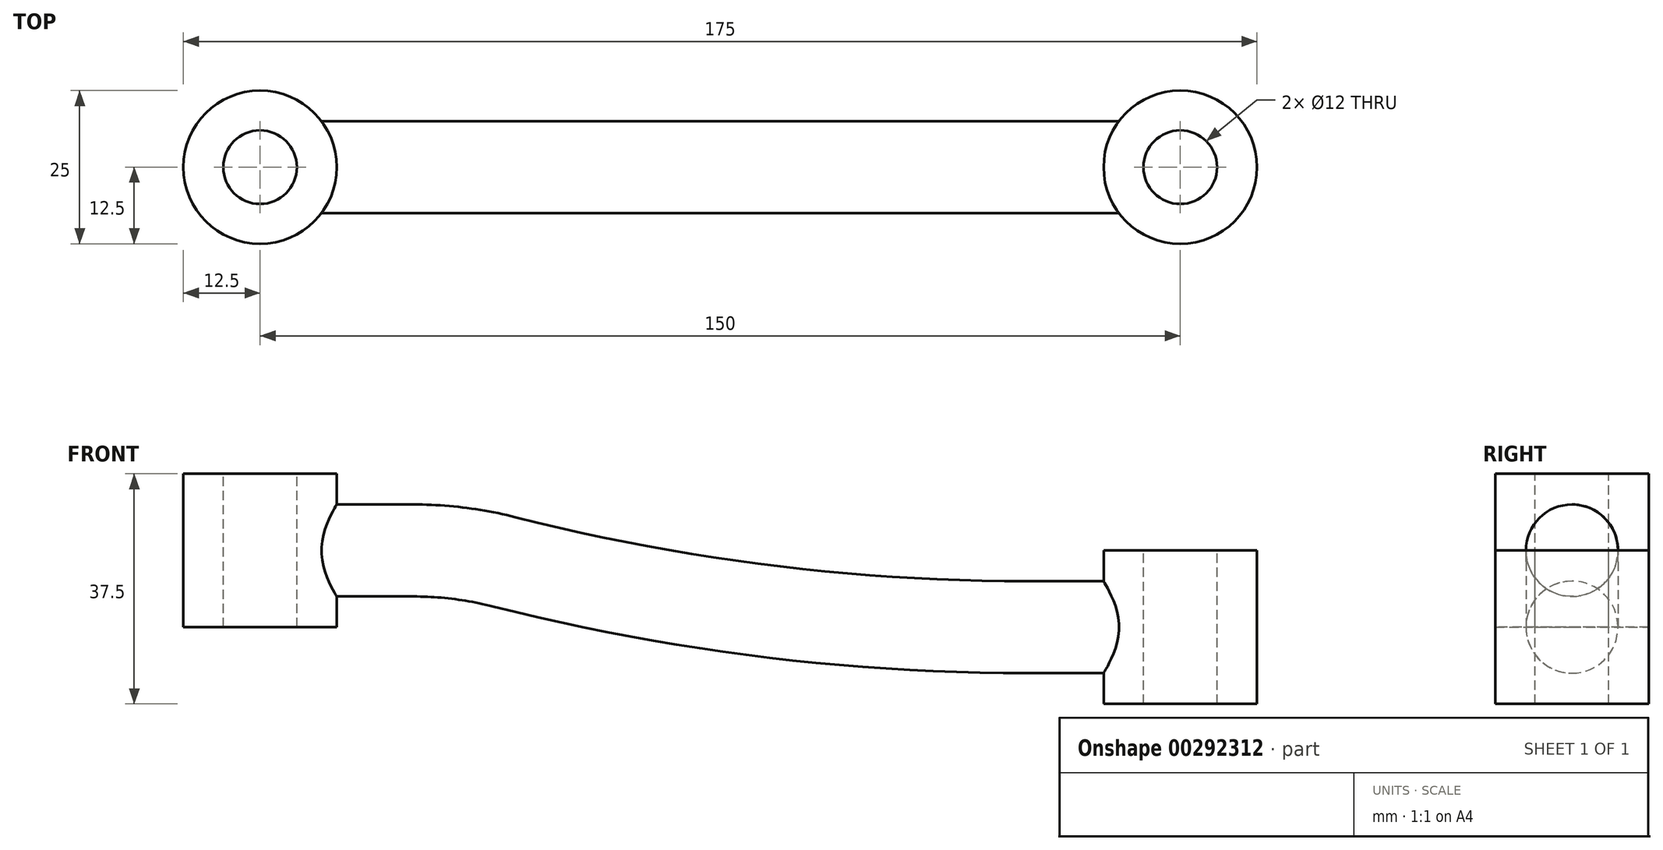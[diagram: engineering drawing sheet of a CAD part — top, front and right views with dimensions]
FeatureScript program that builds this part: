
annotation { "Feature Type Name" : "Feature", "Feature Type Description" : "" }
export const myFeature = defineFeature(function(context is Context, id is Id, definition is map)
    precondition{}
    {
        {
            var Q0;
            Q0=qCreatedBy(makeId("Top.planeOp"),FACE);
            var sketch = newSketch(context, id + "F0", { "sketchPlane" : qUnion([Q0])});
            skCircle(sketch, "E0", {"center": v(0, 0) * mm, "radius": 12.5 * mm});
            skCircle(sketch, "E1", {"center": v(150, 0) * mm, "radius": 12.5 * mm});
            skSolve(sketch);
        }
        {
            var Q0;
            Q0=makeQuery(id+"F0.imprint","IMPRINT",FACE,{"disambiguationData":[TD([[makeQuery(id+"F0.imprint","IMPRINT",EDGE,{"derivedFrom":sQuery(id+"F0.wireOp",EDGE,"E0")}),1.0]])]});
            extrude(context, id + "F1", {"entities" : qUnion([Q0]), "depth" : 25 * mm});
        }
        {
            var Q0;
            Q0=makeQuery(id+"F0.imprint","IMPRINT",FACE,{"disambiguationData":[TD([[makeQuery(id+"F0.imprint","IMPRINT",EDGE,{"derivedFrom":sQuery(id+"F0.wireOp",EDGE,"E1")}),1.0]])]});
            extrude(context, id + "F2", {"entities" : qUnion([Q0]), "endBound" : BoundingType.SYMMETRIC, "depth" : 25 * mm});
        }
        {
            var Q0;
            Q0=qCreatedBy(makeId("Front.planeOp"),FACE);
            var sketch = newSketch(context, id + "F3", { "sketchPlane" : qUnion([Q0])});
            skLineSegment(sketch, "E2", {"start": v(0, 12.5) * mm, "end": v(25, 12.5) * mm});
            skLineSegment(sketch, "E3", {"start": v(150, 0) * mm, "end": v(125, 0) * mm});
            skArc(sketch, "E4", {"start": v(39.77, 10.65) * mm, "mid": v(32.44, 12.04) * mm, "end": v(25, 12.5) * mm});
            skArc(sketch, "E5", {"start": v(39.77, 10.65) * mm, "mid": v(82.05, 2.67) * mm, "end": v(125, 0) * mm});
            skSolve(sketch);
        }
        {
            var Q0;
            Q0=qCreatedBy(makeId("Right.planeOp"),FACE);
            var sketch = newSketch(context, id + "F4", { "sketchPlane" : qUnion([Q0])});
            skCircle(sketch, "E6", {"center": v(0, 12.5) * mm, "radius": 7.5 * mm});
            skSolve(sketch);
        }
        {
            var Q0;
            Q0 = qSketchRegion(id + "F4", true);
            var Q1;
            Q1 = qConstructionFilter(qBodyType(qCreatedBy(id + "F3" ,EDGE), BodyType.WIRE), ConstructionObject.NO);
            sweep(context, id + "F5", {"operationType" : NewBodyOperationType.ADD, "profiles" : qUnion([Q0]), "path" : qUnion([Q1])});
        }
        {
            var Q0;
            Q0=makeQuery(id+"F1.opExtrude","CAP_FACE",FACE,{"disambiguationData":[OSD([sQuery(id+"F0.wireOp",EDGE,"E0")])],"isStart":false});
            var sketch = newSketch(context, id + "F6", { "sketchPlane" : qUnion([Q0])});
            skCircle(sketch, "E7", {"center": v(0, 0) * mm, "radius": 6 * mm});
            skCircle(sketch, "E8", {"center": v(150, 0) * mm, "radius": 6 * mm});
            skSolve(sketch);
        }
        {
            var Q0;
            Q0=makeQuery(id+"F6.imprint","IMPRINT",FACE,{"disambiguationData":[TD([[makeQuery(id+"F6.imprint","IMPRINT",EDGE,{"derivedFrom":sQuery(id+"F6.wireOp",EDGE,"E7")}),1.0]])]});
            var Q1;
            Q1=makeQuery(id+"F6.imprint","IMPRINT",FACE,{"disambiguationData":[TD([[makeQuery(id+"F6.imprint","IMPRINT",EDGE,{"derivedFrom":sQuery(id+"F6.wireOp",EDGE,"E8")}),1.0]])]});
            extrude(context, id + "F7", {"entities" : qUnion([Q0, Q1]), "operationType" : NewBodyOperationType.REMOVE, "endBound" : BoundingType.THROUGH_ALL, "oppositeDirection" : true, "depth" : 25 * mm});
        }
    });
